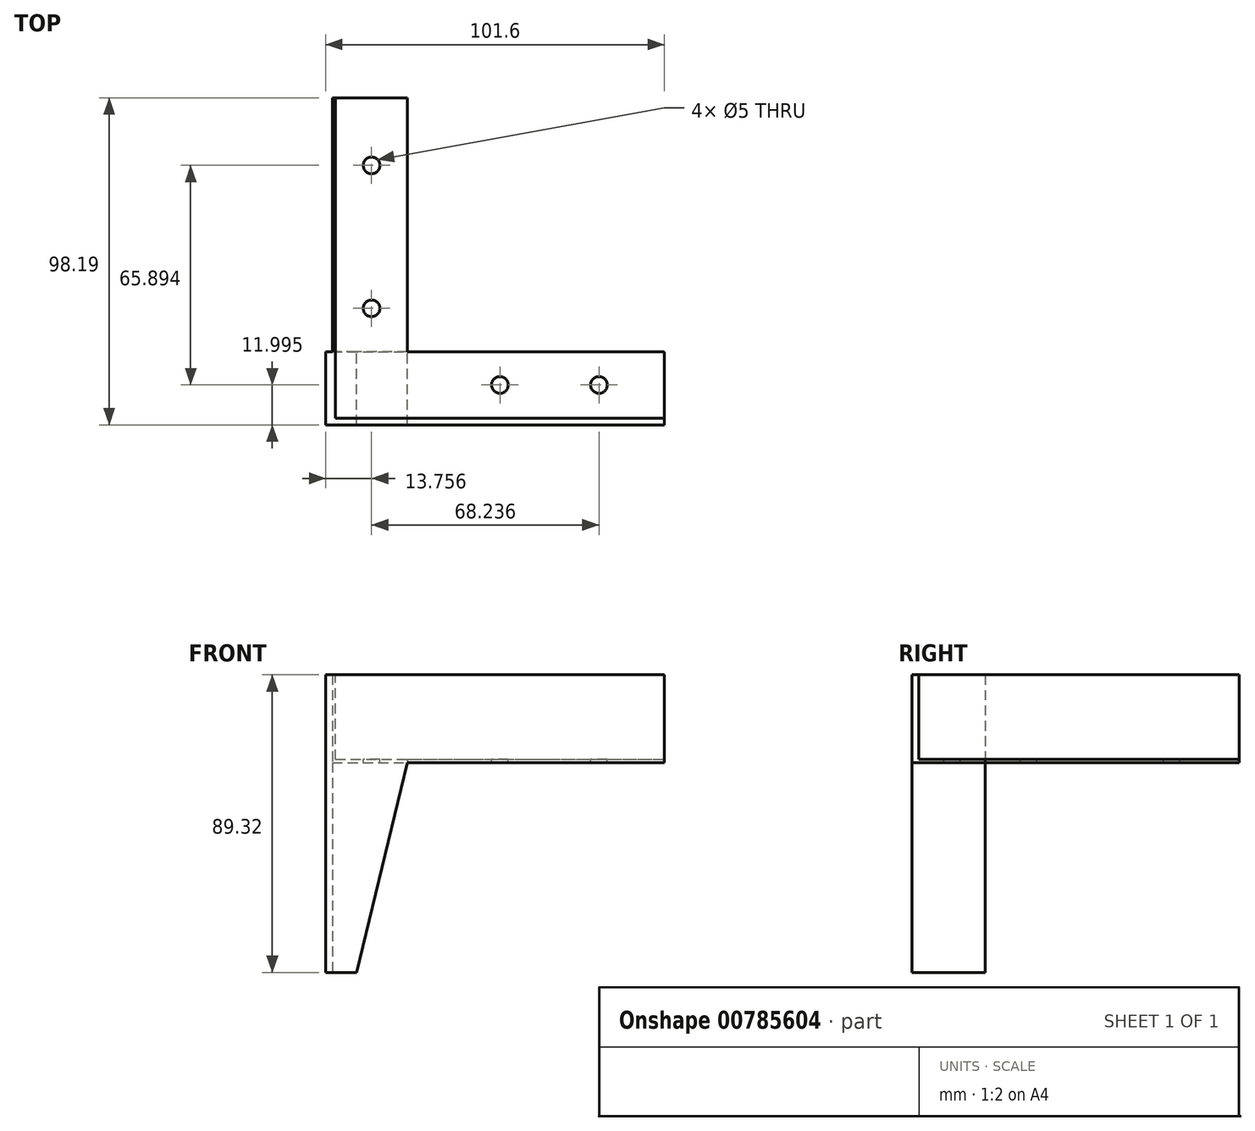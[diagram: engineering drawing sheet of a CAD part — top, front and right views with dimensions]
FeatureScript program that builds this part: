
annotation { "Feature Type Name" : "Feature", "Feature Type Description" : "" }
export const myFeature = defineFeature(function(context is Context, id is Id, definition is map)
    precondition{}
    {
        {
            var Q0;
            Q0=qCreatedBy(makeId("Front.planeOp"),FACE);
            var sketch = newSketch(context, id + "F0", { "sketchPlane" : qUnion([Q0])});
            skLineSegment(sketch, "E0", {"start": v(0, 0) * mm, "end": v(76.2, 0) * mm});
            skLineSegment(sketch, "E1", {"start": v(76.2, 0) * mm, "end": v(76.2, -13.64) * mm});
            skLineSegment(sketch, "E2", {"start": v(76.2, -13.64) * mm, "end": v(24.56, -13.64) * mm});
            skLineSegment(sketch, "E3", {"start": v(24.56, -13.64) * mm, "end": v(9.24, -76.62) * mm});
            skLineSegment(sketch, "E4", {"start": v(9.24, -76.62) * mm, "end": v(0, -76.62) * mm});
            skLineSegment(sketch, "E5", {"start": v(0, -76.62) * mm, "end": v(0, 0) * mm});
            skSolve(sketch);
        }
        {
            var Q0;
            Q0=makeQuery(id+"F0.imprint","IMPRINT",FACE,{"disambiguationData":[TD([[makeQuery(id+"F0.imprint","IMPRINT",EDGE,{"derivedFrom":sQuery(id+"F0.wireOp",EDGE,"E0")}),-1.0]])]});
            extrude(context, id + "F1", {"entities" : qUnion([Q0]), "depth" : 2 * mm, "offsetDistance" : 25.4 * mm});
        }
        {
            var Q0;
            Q0=makeQuery(id+"F1.opExtrude","CAP_FACE",FACE,{"disambiguationData":[OSD([sQuery(id+"F0.wireOp",EDGE,"E0"),sQuery(id+"F0.wireOp",EDGE,"E1"),sQuery(id+"F0.wireOp",EDGE,"E2"),sQuery(id+"F0.wireOp",EDGE,"E3"),sQuery(id+"F0.wireOp",EDGE,"E4"),sQuery(id+"F0.wireOp",EDGE,"E5")])],"isStart":true});
            var sketch = newSketch(context, id + "F2", { "sketchPlane" : qUnion([Q0])});
            skLineSegment(sketch, "E6", {"start": v(-2, 0) * mm, "end": v(-2, -76.62) * mm});
            skPoint(sketch, "E6.endSnap0", {"position": v(-4.62, -76.62) * mm});
            skLineSegment(sketch, "E7", {"start": v(-2, -76.62) * mm, "end": v(0, -76.62) * mm});
            skLineSegment(sketch, "E8", {"start": v(0, -76.62) * mm, "end": v(0, 0) * mm});
            skLineSegment(sketch, "E9", {"start": v(0, 0) * mm, "end": v(-2, 0) * mm});
            skSolve(sketch);
        }
        {
            var Q0;
            Q0=makeQuery(id+"F2.imprint","IMPRINT",FACE,{"disambiguationData":[TD([[makeQuery(id+"F2.imprint","IMPRINT",EDGE,{"derivedFrom":sQuery(id+"F2.wireOp",EDGE,"E6")}),1.0]])]});
            extrude(context, id + "F3", {"entities" : qUnion([Q0]), "operationType" : NewBodyOperationType.ADD, "depth" : 20 * mm, "offsetDistance" : 25.4 * mm});
        }
        {
            var Q0;
            Q0=makeQuery(id+"F1.opExtrude","CAP_FACE",FACE,{"disambiguationData":[OSD([sQuery(id+"F0.wireOp",EDGE,"E0"),sQuery(id+"F0.wireOp",EDGE,"E1"),sQuery(id+"F0.wireOp",EDGE,"E2"),sQuery(id+"F0.wireOp",EDGE,"E3"),sQuery(id+"F0.wireOp",EDGE,"E4"),sQuery(id+"F0.wireOp",EDGE,"E5")])],"isStart":true});
            extrude(context, id + "F4", {"entities" : qUnion([Q0]), "operationType" : NewBodyOperationType.ADD, "depth" : 19.99 * mm, "offsetDistance" : 25.4 * mm});
        }
        {
            var Q0;
            Q0=makeQuery(id+"F4.opExtrude","CAP_FACE",FACE,{"disambiguationData":[OSD([sQuery(id+"F0.wireOp",EDGE,"E0"),sQuery(id+"F0.wireOp",EDGE,"E1"),sQuery(id+"F0.wireOp",EDGE,"E2"),sQuery(id+"F0.wireOp",EDGE,"E3"),sQuery(id+"F0.wireOp",EDGE,"E4"),sQuery(id+"F0.wireOp",EDGE,"E5")])],"isStart":false});
            var sketch = newSketch(context, id + "F5", { "sketchPlane" : qUnion([Q0])});
            skLineSegment(sketch, "E10.0.1", {"start": v(0, 0) * mm, "end": v(0, -76.62) * mm});
            skLineSegment(sketch, "E10.0.3", {"start": v(0, -76.62) * mm, "end": v(0, 0) * mm});
            skLineSegment(sketch, "E11.bottom", {"start": v(0, 0) * mm, "end": v(-24.56, 0) * mm});
            skLineSegment(sketch, "E11.top", {"start": v(0, -13.64) * mm, "end": v(-24.56, -13.64) * mm});
            skLineSegment(sketch, "E11.left", {"start": v(0, 0) * mm, "end": v(0, -13.64) * mm});
            skLineSegment(sketch, "E11.right", {"start": v(-24.56, 0) * mm, "end": v(-24.56, -13.64) * mm});
            skSolve(sketch);
        }
        {
            var Q0;
            {var subQ3=sQuery(id+"F5.wireOp",EDGE,"E11.right");Q0=makeQuery(id+"F5.imprint","IMPRINT",FACE,{"disambiguationData":[TD([[makeQuery(id+"F5.imprint","IMPRINT",EDGE,{"derivedFrom":subQ3}),1.0]])]});}
            var Q1;
            {var subQ3=sQuery(id+"F5.wireOp",EDGE,"E11.left");Q1=makeQuery(id+"F5.imprint","IMPRINT",FACE,{"disambiguationData":[TD([[makeQuery(id+"F5.imprint","IMPRINT",EDGE,{"derivedFrom":subQ3}),-1.0]])]});}
            extrude(context, id + "F6", {"entities" : qUnion([Q0, Q1]), "operationType" : NewBodyOperationType.ADD, "depth" : 76.2 * mm, "offsetDistance" : 25.4 * mm});
        }
        {
            var Q0;
            {var subQ0=sQuery(id+"F0.wireOp",EDGE,"E1");Q0=makeQuery(id+"F4.boolean.opBoolean","MERGE",FACE,{"derivedFrom":[makeQuery(id+"F1.opExtrude","SWEPT_FACE",FACE,{"disambiguationData":[OSD([subQ0])]}),makeQuery(id+"F4.opExtrude","SWEPT_FACE",FACE,{"disambiguationData":[OSD([subQ0])]})]});}
            extrude(context, id + "F7", {"entities" : qUnion([Q0]), "operationType" : NewBodyOperationType.ADD, "depth" : 25.4 * mm, "offsetDistance" : 25.4 * mm});
        }
        {
            var Q0;
            {var subQ0=sQuery(id+"F0.wireOp",EDGE,"E0");Q0=makeQuery(id+"F7.boolean.opBoolean","MERGE",FACE,{"derivedFrom":[makeQuery(id+"F6.boolean.opBoolean","MERGE",FACE,{"derivedFrom":[makeQuery(id+"F4.boolean.opBoolean","MERGE",FACE,{"derivedFrom":[makeQuery(id+"F3.boolean.opBoolean","MERGE",FACE,{"derivedFrom":[makeQuery(id+"F1.opExtrude","SWEPT_FACE",FACE,{"disambiguationData":[OSD([subQ0])]}),makeQuery(id+"F3.opExtrude","SWEPT_FACE",FACE,{"disambiguationData":[OSD([sQuery(id+"F2.wireOp",EDGE,"E9")])]})]}),makeQuery(id+"F4.opExtrude","SWEPT_FACE",FACE,{"disambiguationData":[OSD([subQ0])]})]}),makeQuery(id+"F6.opExtrude","SWEPT_FACE",FACE,{"disambiguationData":[OSD([sQuery(id+"F5.wireOp",EDGE,"E11.bottom")])]})]}),makeQuery(id+"F7.opExtrude","SWEPT_FACE",FACE,{"disambiguationData":[OSD([subQ0,sQuery(id+"F0.wireOp",EDGE,"E1")])]})]});}
            var sketch = newSketch(context, id + "F8", { "sketchPlane" : qUnion([Q0])});
            skLineSegment(sketch, "E12.0", {"start": v(101.6, -2) * mm, "end": v(101.6, 19.99) * mm});
            skLineSegment(sketch, "E13.0", {"start": v(24.56, 19.99) * mm, "end": v(101.6, 19.99) * mm});
            skLineSegment(sketch, "E14.0", {"start": v(24.56, 96.19) * mm, "end": v(24.56, 19.99) * mm});
            skLineSegment(sketch, "E15.0", {"start": v(0, 96.19) * mm, "end": v(24.56, 96.19) * mm});
            skLineSegment(sketch, "E16", {"start": v(2.95, 96.19) * mm, "end": v(2.95, 0) * mm});
            skLineSegment(sketch, "E17", {"start": v(2.95, 0) * mm, "end": v(101.6, 0) * mm});
            skSolve(sketch);
        }
        {
            var Q0;
            {var subQ3=sQuery(id+"F8.wireOp",EDGE,"E13.0");Q0=makeQuery(id+"F8.imprint","IMPRINT",FACE,{"disambiguationData":[TD([[makeQuery(id+"F8.imprint","IMPRINT",EDGE,{"derivedFrom":subQ3}),-1.0]])]});}
            extrude(context, id + "F9", {"entities" : qUnion([Q0]), "operationType" : NewBodyOperationType.REMOVE, "oppositeDirection" : true, "depth" : 12.7 * mm, "offsetDistance" : 25.4 * mm});
        }
        {
            var Q0;
            {var subQ0=sQuery(id+"F0.wireOp",EDGE,"E0");Q0=makeQuery(id+"F7.boolean.opBoolean","MERGE",FACE,{"derivedFrom":[makeQuery(id+"F6.boolean.opBoolean","MERGE",FACE,{"derivedFrom":[makeQuery(id+"F4.boolean.opBoolean","MERGE",FACE,{"derivedFrom":[makeQuery(id+"F3.boolean.opBoolean","MERGE",FACE,{"derivedFrom":[makeQuery(id+"F1.opExtrude","SWEPT_FACE",FACE,{"disambiguationData":[OSD([subQ0])]}),makeQuery(id+"F3.opExtrude","SWEPT_FACE",FACE,{"disambiguationData":[OSD([sQuery(id+"F2.wireOp",EDGE,"E9")])]})]}),makeQuery(id+"F4.opExtrude","SWEPT_FACE",FACE,{"disambiguationData":[OSD([subQ0])]})]}),makeQuery(id+"F6.opExtrude","SWEPT_FACE",FACE,{"disambiguationData":[OSD([sQuery(id+"F5.wireOp",EDGE,"E11.bottom")])]})]}),makeQuery(id+"F7.opExtrude","SWEPT_FACE",FACE,{"disambiguationData":[OSD([subQ0,sQuery(id+"F0.wireOp",EDGE,"E1")])]})]});}
            extrude(context, id + "F10", {"entities" : qUnion([Q0]), "operationType" : NewBodyOperationType.ADD, "depth" : 12.7 * mm, "offsetDistance" : 25.4 * mm});
        }
        {
            var Q0;
            Q0=makeQuery(id+"F9.boolean.opBoolean","COPY",FACE,{"derivedFrom":makeQuery(id+"F9.opExtrude","CAP_FACE",FACE,{"disambiguationData":[OSD([sQuery(id+"F8.wireOp",EDGE,"E12.0"),sQuery(id+"F8.wireOp",EDGE,"E13.0"),sQuery(id+"F8.wireOp",EDGE,"E14.0"),sQuery(id+"F8.wireOp",EDGE,"E15.0"),sQuery(id+"F8.wireOp",EDGE,"E16"),sQuery(id+"F8.wireOp",EDGE,"E17")])],"isStart":false})});
            var sketch = newSketch(context, id + "F11", { "sketchPlane" : qUnion([Q0])});
            skLineSegment(sketch, "E18", {"start": v(101.6, 10) * mm, "end": v(2.95, 10) * mm});
            skLineSegment(sketch, "E19", {"start": v(13.76, 96.19) * mm, "end": v(13.76, 10) * mm});
            skCircle(sketch, "E20", {"center": v(82, 10) * mm, "radius": 2.5 * mm, "construction": true});
            skCircle(sketch, "E21", {"center": v(52.28, 10) * mm, "radius": 2.53 * mm});
            skCircle(sketch, "E22", {"center": v(13.76, 75.89) * mm, "radius": 3.2 * mm});
            skCircle(sketch, "E23", {"center": v(13.76, 33) * mm, "radius": 3.44 * mm});
            skSolve(sketch);
        }
        {
            var Q0;
            Q0=sQuery(id+"F11.wireOp",VERTEX,"E20.center");
            var Q1;
            Q1=sQuery(id+"F11.wireOp",VERTEX,"E21.center");
            var Q2;
            Q2=sQuery(id+"F11.wireOp",VERTEX,"E23.center");
            var Q3;
            Q3=sQuery(id+"F11.wireOp",VERTEX,"E22.center");
            var Q4;
            Q4=makeQuery(id+"F1.opExtrude","SWEPT_BODY",BODY,{"disambiguationData":[OSD([sQuery(id+"F0.wireOp",EDGE,"E0"),sQuery(id+"F0.wireOp",EDGE,"E1"),sQuery(id+"F0.wireOp",EDGE,"E2"),sQuery(id+"F0.wireOp",EDGE,"E3"),sQuery(id+"F0.wireOp",EDGE,"E4"),sQuery(id+"F0.wireOp",EDGE,"E5")])]});
            hole(context, id + "F12", {"style" : HoleStyle.SIMPLE, "endStyle" : HoleEndStyle.THROUGH, "holeDiameter" : 5 * mm, "majorDiameter" : 5 * mm, "isTappedThrough" : true, "tappedDepth" : 12 * mm, "tapClearance" : 3, "locations" : qUnion([Q0, Q1, Q2, Q3]), "scope" : qUnion([Q4])});
        }
    });
